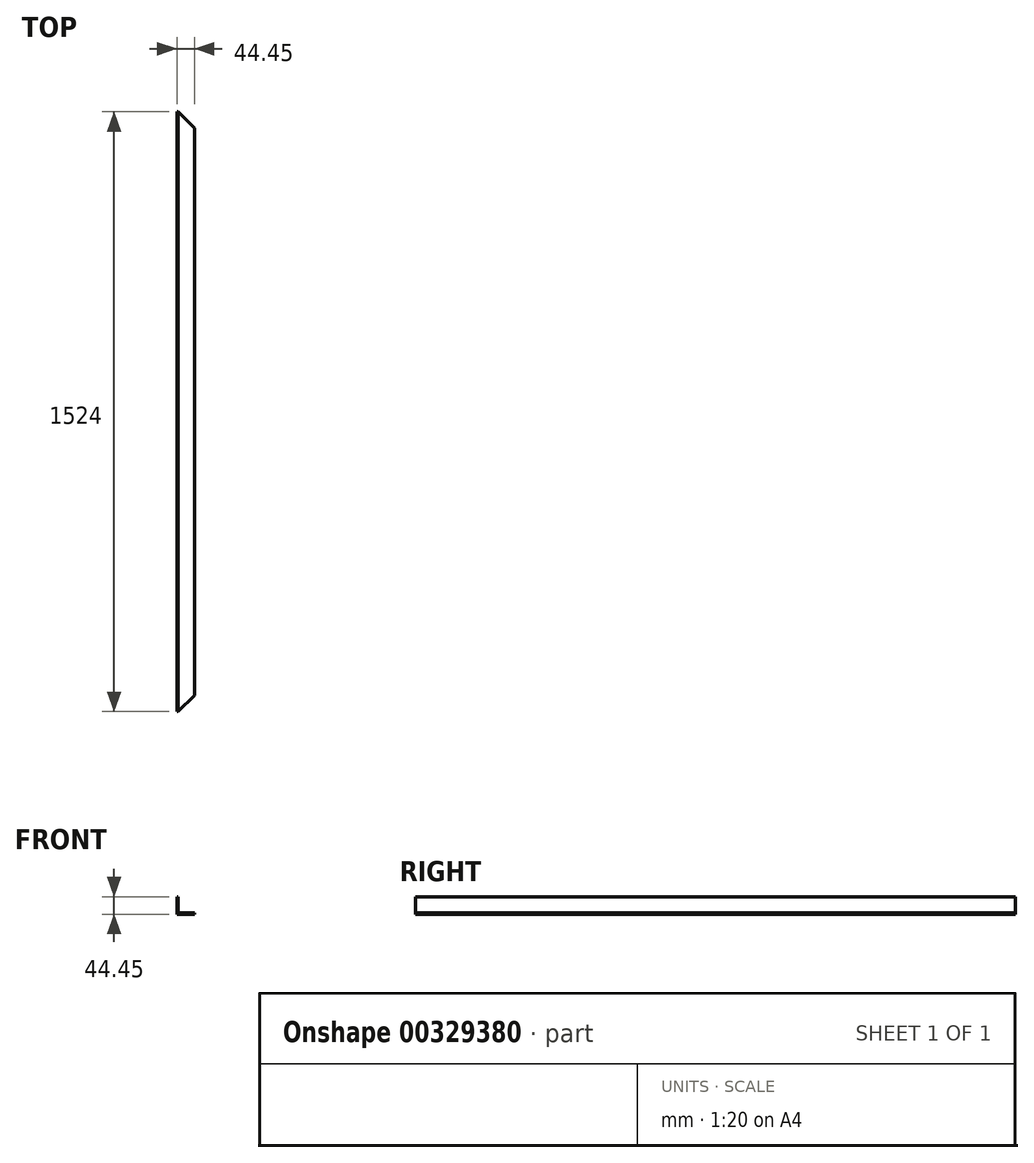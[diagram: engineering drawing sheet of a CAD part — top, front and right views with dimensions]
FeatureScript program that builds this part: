
annotation { "Feature Type Name" : "Feature", "Feature Type Description" : "" }
export const myFeature = defineFeature(function(context is Context, id is Id, definition is map)
    precondition{}
    {
        {
            var Q0;
            Q0=qCreatedBy(makeId("Front.planeOp"),FACE);
            var sketch = newSketch(context, id + "F0", { "sketchPlane" : qUnion([Q0])});
            skLineSegment(sketch, "E0", {"start": v(-53.88, 29.97) * mm, "end": v(-53.88, -14.48) * mm});
            skLineSegment(sketch, "E1", {"start": v(-53.88, -14.48) * mm, "end": v(-9.43, -14.48) * mm});
            skLineSegment(sketch, "E2.0", {"start": v(-50.7, -11.3) * mm, "end": v(-9.43, -11.3) * mm});
            skLineSegment(sketch, "E2.1", {"start": v(-50.7, 29.97) * mm, "end": v(-50.7, -11.3) * mm});
            skLineSegment(sketch, "E3", {"start": v(-53.88, 29.97) * mm, "end": v(-50.7, 29.97) * mm});
            skLineSegment(sketch, "E4", {"start": v(-9.43, -11.3) * mm, "end": v(-9.43, -14.48) * mm});
            skSolve(sketch);
        }
        {
            var Q0;
            Q0=makeQuery(id+"F0.imprint","IMPRINT",FACE,{"disambiguationData":[TD([[makeQuery(id+"F0.imprint","IMPRINT",EDGE,{"derivedFrom":sQuery(id+"F0.wireOp",EDGE,"E0")}),1.0]])]});
            extrude(context, id + "F1", {"entities" : qUnion([Q0]), "depth" : 1524 * mm});
        }
        {
            var Q0;
            Q0=makeQuery(id+"F1.opExtrude","SWEPT_FACE",FACE,{"disambiguationData":[OSD([sQuery(id+"F0.wireOp",EDGE,"E2.0")])]});
            var sketch = newSketch(context, id + "F2", { "sketchPlane" : qUnion([Q0])});
            skLineSegment(sketch, "E5", {"start": v(-9.43, -41.34) * mm, "end": v(-50.7, 0) * mm});
            skSolve(sketch);
        }
        {
            var Q0;
            {var subQ0=sQuery(id+"F2.wireOp",EDGE,"E5");Q0=makeQuery(id+"F2.imprint","IMPRINT",FACE,{"disambiguationData":[TD([[makeQuery(id+"F2.imprint","IMPRINT",EDGE,{"derivedFrom":subQ0}),-1.0]])]});}
            extrude(context, id + "F3", {"entities" : qUnion([Q0]), "operationType" : NewBodyOperationType.REMOVE, "oppositeDirection" : true, "depth" : 25.4 * mm});
        }
        {
            var Q0;
            Q0=makeQuery(id+"F1.opExtrude","SWEPT_FACE",FACE,{"disambiguationData":[OSD([sQuery(id+"F0.wireOp",EDGE,"E2.0")])]});
            var sketch = newSketch(context, id + "F4", { "sketchPlane" : qUnion([Q0])});
            skLineSegment(sketch, "E6", {"start": v(-9.43, -1482.73) * mm, "end": v(-50.7, -1524) * mm});
            skSolve(sketch);
        }
        {
            var Q0;
            {var subQ0=sQuery(id+"F4.wireOp",EDGE,"E6");Q0=makeQuery(id+"F4.imprint","IMPRINT",FACE,{"disambiguationData":[TD([[makeQuery(id+"F4.imprint","IMPRINT",EDGE,{"derivedFrom":subQ0}),1.0]])]});}
            extrude(context, id + "F5", {"entities" : qUnion([Q0]), "operationType" : NewBodyOperationType.REMOVE, "oppositeDirection" : true, "depth" : 25.4 * mm});
        }
    });
